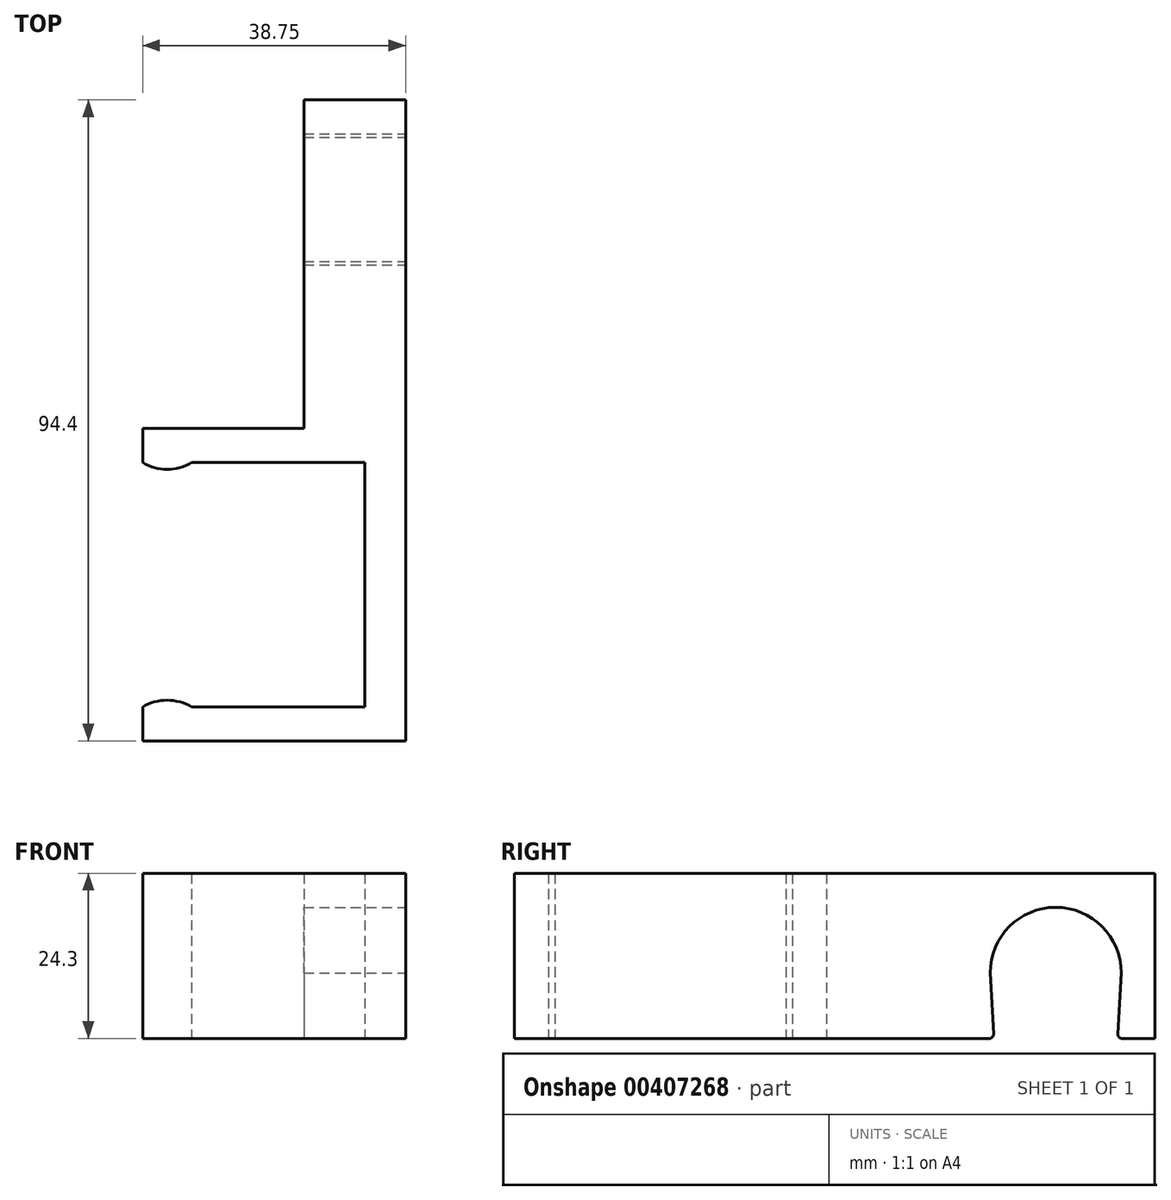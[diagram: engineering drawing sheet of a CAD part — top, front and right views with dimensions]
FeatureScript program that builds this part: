
annotation { "Feature Type Name" : "Feature", "Feature Type Description" : "" }
export const myFeature = defineFeature(function(context is Context, id is Id, definition is map)
    precondition{}
    {
        {
            var Q0;
            Q0=qCreatedBy(makeId("Top.planeOp"),FACE);
            var sketch = newSketch(context, id + "F0", { "sketchPlane" : qUnion([Q0])});
            skLineSegment(sketch, "E0", {"start": v(7.22, 0) * mm, "end": v(32.75, 0) * mm});
            skLineSegment(sketch, "E1", {"start": v(32.75, 0) * mm, "end": v(32.75, -36) * mm});
            skLineSegment(sketch, "E2", {"start": v(32.75, -36) * mm, "end": v(7.22, -36) * mm});
            skLineSegment(sketch, "E3", {"start": v(0, -36) * mm, "end": v(0, -41) * mm});
            skLineSegment(sketch, "E4", {"start": v(0, -41) * mm, "end": v(38.75, -41) * mm});
            skLineSegment(sketch, "E5", {"start": v(38.75, -41) * mm, "end": v(38.75, 53.4) * mm});
            skLineSegment(sketch, "E6", {"start": v(38.75, 53.4) * mm, "end": v(23.75, 53.4) * mm});
            skLineSegment(sketch, "E7", {"start": v(23.75, 53.4) * mm, "end": v(23.75, 5) * mm});
            skLineSegment(sketch, "E8", {"start": v(23.75, 5) * mm, "end": v(0, 5) * mm});
            skLineSegment(sketch, "E9", {"start": v(0, 5) * mm, "end": v(0, 0) * mm});
            skArc(sketch, "E10", {"start": v(0, 0) * mm, "mid": v(3.6, -1) * mm, "end": v(7.22, 0) * mm});
            skLineSegment(sketch, "E11", {"start": v(32.75, -18) * mm, "end": v(13.54, -18) * mm, "construction": true});
            skArc(sketch, "E12.MirrorCS", {"start": v(0, -36) * mm, "mid": v(3.6, -35) * mm, "end": v(7.22, -36) * mm});
            skSolve(sketch);
        }
        {
            var Q0;
            Q0 = qSketchRegion(id + "F0", true);
            extrude(context, id + "F1", {"entities" : qUnion([Q0]), "depth" : (5 + 19.3) * mm});
        }
        {
            var Q0;
            Q0=makeQuery(id+"F1.opExtrude","SWEPT_FACE",FACE,{"disambiguationData":[OSD([sQuery(id+"F0.wireOp",EDGE,"E5")])]});
            var sketch = newSketch(context, id + "F2", { "sketchPlane" : qUnion([Q0])});
            skArc(sketch, "E13", {"start": v(48.4, 9.65) * mm, "mid": v(38.75, 19.3) * mm, "end": v(29.1, 9.65) * mm});
            skLineSegment(sketch, "E14", {"start": v(48.4, 9.65) * mm, "end": v(48.4, 0) * mm, "construction": true});
            skLineSegment(sketch, "E15", {"start": v(29.1, 9.65) * mm, "end": v(29.1, 0) * mm, "construction": true});
            skLineSegment(sketch, "E16", {"start": v(48.4, 9.65) * mm, "end": v(47.9, 0.68) * mm});
            skArc(sketch, "E17", {"start": v(47.9, 0.68) * mm, "mid": v(48.03, 0.25) * mm, "end": v(48.4, 0) * mm});
            skLineSegment(sketch, "E18", {"start": v(38.75, 9.65) * mm, "end": v(38.75, 6.16) * mm, "construction": true});
            skArc(sketch, "E19.MirrorCS", {"start": v(29.6, 0.68) * mm, "mid": v(29.47, 0.25) * mm, "end": v(29.1, 0) * mm});
            skLineSegment(sketch, "E20.MirrorCS", {"start": v(29.1, 9.65) * mm, "end": v(29.6, 0.68) * mm});
            skLineSegment(sketch, "E21", {"start": v(48.4, 0) * mm, "end": v(29.1, 0) * mm});
            skSolve(sketch);
        }
        {
            var Q0;
            Q0 = qSketchRegion(id + "F2", true);
            extrude(context, id + "F3", {"entities" : qUnion([Q0]), "operationType" : NewBodyOperationType.REMOVE, "oppositeDirection" : true, "depth" : 25 * mm});
        }
    });
